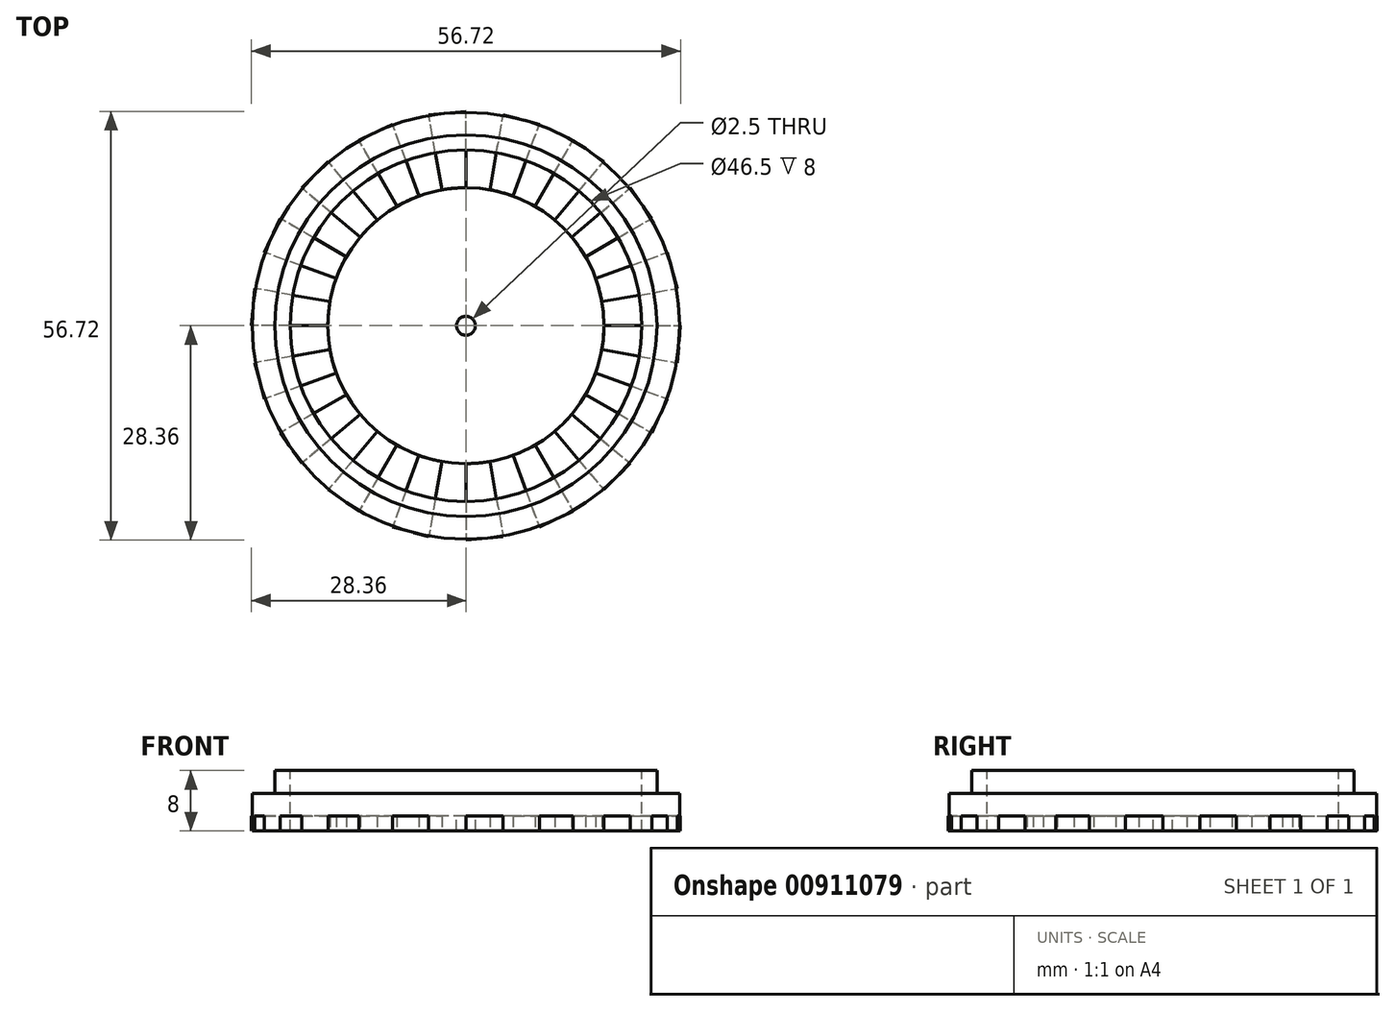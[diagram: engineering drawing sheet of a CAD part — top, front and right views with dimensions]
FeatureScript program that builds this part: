
annotation { "Feature Type Name" : "Feature", "Feature Type Description" : "" }
export const myFeature = defineFeature(function(context is Context, id is Id, definition is map)
    precondition{}
    {
        {
            var Q0;
            Q0=qCreatedBy(makeId("Front.planeOp"),FACE);
            var sketch = newSketch(context, id + "F0", { "sketchPlane" : qUnion([Q0])});
            skLineSegment(sketch, "E0", {"start": v(-103.65, 0) * mm, "end": v(117.55, 0) * mm, "construction": true});
            skLineSegment(sketch, "E1", {"start": v(0, 46.85) * mm, "end": v(0, -57.43) * mm, "construction": true});
            skLineSegment(sketch, "E2.bottom", {"start": v(-1.25, 2) * mm, "end": v(-18.25, 2) * mm});
            skLineSegment(sketch, "E2.top", {"start": v(-1.25, 0) * mm, "end": v(-18.25, 0) * mm});
            skLineSegment(sketch, "E2.left", {"start": v(-1.25, 2) * mm, "end": v(-1.25, 0) * mm});
            skLineSegment(sketch, "E2.right", {"start": v(-18.25, 2) * mm, "end": v(-18.25, 0) * mm});
            skLineSegment(sketch, "E3.top", {"start": v(-23.25, 0) * mm, "end": v(-25.25, 0) * mm});
            skLineSegment(sketch, "E4", {"start": v(-106.04, 1) * mm, "end": v(129.67, 1) * mm, "construction": true});
            skLineSegment(sketch, "E5", {"start": v(-23.25, 0) * mm, "end": v(-23.25, 8) * mm});
            skLineSegment(sketch, "E6", {"start": v(-25.25, 8) * mm, "end": v(-25.25, 0) * mm});
            skLineSegment(sketch, "E7", {"start": v(-25.25, 8) * mm, "end": v(-23.25, 8) * mm});
            skLineSegment(sketch, "E8.bottom", {"start": v(-25.25, 0) * mm, "end": v(-28.25, 0) * mm});
            skLineSegment(sketch, "E8.top", {"start": v(-25.25, 5) * mm, "end": v(-28.25, 5) * mm});
            skLineSegment(sketch, "E8.left", {"start": v(-25.25, 0) * mm, "end": v(-25.25, 5) * mm});
            skLineSegment(sketch, "E8.right", {"start": v(-28.25, 0) * mm, "end": v(-28.25, 5) * mm});
            skLineSegment(sketch, "E9.MirrorCS", {"start": v(1.25, 2) * mm, "end": v(18.25, 2) * mm});
            skLineSegment(sketch, "E10.MirrorCS", {"start": v(1.25, 2) * mm, "end": v(1.25, 0) * mm});
            skLineSegment(sketch, "E11.MirrorCS", {"start": v(28.25, 0) * mm, "end": v(28.25, 5) * mm});
            skLineSegment(sketch, "E12.MirrorCS", {"start": v(25.25, 8) * mm, "end": v(25.25, 0) * mm});
            skLineSegment(sketch, "E13.MirrorCS", {"start": v(1.25, 0) * mm, "end": v(18.25, 0) * mm});
            skLineSegment(sketch, "E14.MirrorCS", {"start": v(25.25, 8) * mm, "end": v(23.25, 8) * mm});
            skLineSegment(sketch, "E15.MirrorCS", {"start": v(25.25, 0) * mm, "end": v(25.25, 5) * mm});
            skLineSegment(sketch, "E16.MirrorCS", {"start": v(25.25, 0) * mm, "end": v(28.25, 0) * mm});
            skLineSegment(sketch, "E17.MirrorCS", {"start": v(25.25, 5) * mm, "end": v(28.25, 5) * mm});
            skLineSegment(sketch, "E18.MirrorCS", {"start": v(18.25, 2) * mm, "end": v(18.25, 0) * mm});
            skLineSegment(sketch, "E19.MirrorCS", {"start": v(23.25, 0) * mm, "end": v(23.25, 8) * mm});
            skLineSegment(sketch, "E20.MirrorCS", {"start": v(23.25, 0) * mm, "end": v(25.25, 0) * mm});
            skSolve(sketch);
        }
        {
            var Q0;
            Q0=makeQuery(id+"F0.imprint","IMPRINT",FACE,{"disambiguationData":[TD([[makeQuery(id+"F0.imprint","IMPRINT",EDGE,{"derivedFrom":sQuery(id+"F0.wireOp",EDGE,"E2.bottom")}),1.0]])]});
            var Q1;
            Q1=makeQuery(id+"F0.imprint","IMPRINT",FACE,{"disambiguationData":[TD([[makeQuery(id+"F0.imprint","IMPRINT",EDGE,{"derivedFrom":sQuery(id+"F0.wireOp",EDGE,"E3.top")}),-1.0]])]});
            var Q2;
            Q2=makeQuery(id+"F0.imprint","IMPRINT",FACE,{"disambiguationData":[TD([[makeQuery(id+"F0.imprint","IMPRINT",EDGE,{"derivedFrom":sQuery(id+"F0.wireOp",EDGE,"E8.bottom")}),-1.0]])]});
            var Q3;
            Q3=sQuery(id+"F0.wireOp",EDGE,"E1");
            revolve(context, id + "F1", {"surfaceOperationType" : NewSurfaceOperationType.NEW, "entities" : qUnion([Q0, Q1, Q2]), "axis" : qUnion([Q3]), "revolveType" : RevolveType.FULL});
        }
        {
            var Q0;
            Q0=makeQuery(id+"F1.opRevolve","SWEPT_FACE",FACE,{"disambiguationData":[OSD([sQuery(id+"F0.wireOp",EDGE,"E2.top")])]});
            var sketch = newSketch(context, id + "F2", { "sketchPlane" : qUnion([Q0])});
            skLineSegment(sketch, "E21", {"start": v(0, -18.25) * mm, "end": v(0, -28.36) * mm});
            skLineSegment(sketch, "E22.1.0", {"start": v(3.17, -17.97) * mm, "end": v(4.92, -27.92) * mm});
            skLineSegment(sketch, "E22.2.0", {"start": v(6.24, -17.15) * mm, "end": v(9.7, -26.65) * mm});
            skLineSegment(sketch, "E22.3.0", {"start": v(9.12, -15.8) * mm, "end": v(14.18, -24.56) * mm});
            skLineSegment(sketch, "E22.4.0", {"start": v(11.73, -13.98) * mm, "end": v(18.23, -21.72) * mm});
            skLineSegment(sketch, "E22.5.0", {"start": v(13.98, -11.73) * mm, "end": v(21.72, -18.23) * mm});
            skLineSegment(sketch, "E22.6.0", {"start": v(15.8, -9.12) * mm, "end": v(24.56, -14.18) * mm});
            skLineSegment(sketch, "E22.7.0", {"start": v(17.15, -6.24) * mm, "end": v(26.65, -9.7) * mm});
            skLineSegment(sketch, "E22.8.0", {"start": v(17.97, -3.17) * mm, "end": v(27.92, -4.92) * mm});
            skLineSegment(sketch, "E22.9.0", {"start": v(18.25, 0) * mm, "end": v(28.36, 0) * mm});
            skLineSegment(sketch, "E22.10.0", {"start": v(17.97, 3.17) * mm, "end": v(27.92, 4.92) * mm});
            skLineSegment(sketch, "E22.11.0", {"start": v(17.15, 6.24) * mm, "end": v(26.65, 9.7) * mm});
            skLineSegment(sketch, "E22.12.0", {"start": v(15.8, 9.13) * mm, "end": v(24.56, 14.18) * mm});
            skLineSegment(sketch, "E22.13.0", {"start": v(13.98, 11.73) * mm, "end": v(21.72, 18.23) * mm});
            skLineSegment(sketch, "E22.14.0", {"start": v(11.73, 13.98) * mm, "end": v(18.23, 21.72) * mm});
            skLineSegment(sketch, "E22.15.0", {"start": v(9.13, 15.8) * mm, "end": v(14.18, 24.56) * mm});
            skLineSegment(sketch, "E22.16.0", {"start": v(6.24, 17.15) * mm, "end": v(9.7, 26.65) * mm});
            skLineSegment(sketch, "E22.17.0", {"start": v(3.17, 17.97) * mm, "end": v(4.92, 27.92) * mm});
            skLineSegment(sketch, "E22.18.0", {"start": v(0, 18.25) * mm, "end": v(0, 28.36) * mm});
            skLineSegment(sketch, "E22.19.0", {"start": v(-3.17, 17.97) * mm, "end": v(-4.92, 27.92) * mm});
            skLineSegment(sketch, "E22.20.0", {"start": v(-6.24, 17.15) * mm, "end": v(-9.7, 26.65) * mm});
            skLineSegment(sketch, "E22.21.0", {"start": v(-9.13, 15.8) * mm, "end": v(-14.18, 24.56) * mm});
            skLineSegment(sketch, "E22.22.0", {"start": v(-11.73, 13.98) * mm, "end": v(-18.23, 21.72) * mm});
            skLineSegment(sketch, "E22.23.0", {"start": v(-13.98, 11.73) * mm, "end": v(-21.72, 18.23) * mm});
            skLineSegment(sketch, "E22.24.0", {"start": v(-15.8, 9.13) * mm, "end": v(-24.56, 14.18) * mm});
            skLineSegment(sketch, "E22.25.0", {"start": v(-17.15, 6.24) * mm, "end": v(-26.65, 9.7) * mm});
            skLineSegment(sketch, "E22.26.0", {"start": v(-17.97, 3.17) * mm, "end": v(-27.92, 4.92) * mm});
            skLineSegment(sketch, "E22.27.0", {"start": v(-18.25, 0) * mm, "end": v(-28.36, 0) * mm});
            skLineSegment(sketch, "E22.28.0", {"start": v(-17.97, -3.17) * mm, "end": v(-27.92, -4.92) * mm});
            skLineSegment(sketch, "E22.29.0", {"start": v(-17.15, -6.24) * mm, "end": v(-26.65, -9.7) * mm});
            skLineSegment(sketch, "E22.30.0", {"start": v(-15.8, -9.12) * mm, "end": v(-24.56, -14.18) * mm});
            skLineSegment(sketch, "E22.31.0", {"start": v(-13.98, -11.73) * mm, "end": v(-21.72, -18.23) * mm});
            skLineSegment(sketch, "E22.32.0", {"start": v(-11.73, -13.98) * mm, "end": v(-18.23, -21.72) * mm});
            skLineSegment(sketch, "E22.33.0", {"start": v(-9.12, -15.8) * mm, "end": v(-14.18, -24.56) * mm});
            skLineSegment(sketch, "E22.34.0", {"start": v(-6.24, -17.15) * mm, "end": v(-9.7, -26.65) * mm});
            skLineSegment(sketch, "E22.35.0", {"start": v(-3.17, -17.97) * mm, "end": v(-4.92, -27.92) * mm});
            skPoint(sketch, "E22.center", {"position": v(0, 0) * mm});
            skLineSegment(sketch, "E23", {"start": v(0, -28.36) * mm, "end": v(-4.92, -27.92) * mm});
            skLineSegment(sketch, "E24", {"start": v(9.7, -26.65) * mm, "end": v(4.92, -27.92) * mm});
            skLineSegment(sketch, "E25", {"start": v(18.23, -21.72) * mm, "end": v(14.18, -24.56) * mm});
            skLineSegment(sketch, "E26", {"start": v(24.56, -14.18) * mm, "end": v(21.72, -18.23) * mm});
            skLineSegment(sketch, "E27", {"start": v(27.92, -4.92) * mm, "end": v(26.65, -9.7) * mm});
            skLineSegment(sketch, "E28", {"start": v(27.92, 4.92) * mm, "end": v(28.36, 0) * mm});
            skLineSegment(sketch, "E29", {"start": v(24.56, 14.18) * mm, "end": v(26.65, 9.7) * mm});
            skLineSegment(sketch, "E30", {"start": v(18.23, 21.72) * mm, "end": v(21.72, 18.23) * mm});
            skLineSegment(sketch, "E31", {"start": v(14.18, 24.56) * mm, "end": v(9.7, 26.65) * mm});
            skLineSegment(sketch, "E32", {"start": v(4.92, 27.92) * mm, "end": v(0, 28.36) * mm});
            skLineSegment(sketch, "E33", {"start": v(-4.92, 27.92) * mm, "end": v(-9.7, 26.65) * mm});
            skLineSegment(sketch, "E34", {"start": v(-14.18, 24.56) * mm, "end": v(-18.23, 21.72) * mm});
            skLineSegment(sketch, "E35", {"start": v(-21.72, 18.23) * mm, "end": v(-24.56, 14.18) * mm});
            skLineSegment(sketch, "E36", {"start": v(-26.65, 9.7) * mm, "end": v(-27.92, 4.92) * mm});
            skLineSegment(sketch, "E37", {"start": v(-28.36, 0) * mm, "end": v(-27.92, -4.92) * mm});
            skLineSegment(sketch, "E38", {"start": v(-26.65, -9.7) * mm, "end": v(-24.56, -14.18) * mm});
            skLineSegment(sketch, "E39", {"start": v(-21.72, -18.23) * mm, "end": v(-18.23, -21.72) * mm});
            skLineSegment(sketch, "E40", {"start": v(-14.18, -24.56) * mm, "end": v(-9.7, -26.65) * mm});
            skSolve(sketch);
        }
        {
            var Q0;
            {var subQ0=sQuery(id+"F2.wireOp",EDGE,"E22.3.0");Q0=makeQuery(id+"F2.imprint","IMPRINT",FACE,{"disambiguationData":[TD([[makeQuery(id+"F2.imprint","IMPRINT",EDGE,{"derivedFrom":subQ0}),1.0]])]});}
            var Q1;
            {var subQ0=sQuery(id+"F2.wireOp",EDGE,"E22.1.0");Q1=makeQuery(id+"F2.imprint","IMPRINT",FACE,{"disambiguationData":[TD([[makeQuery(id+"F2.imprint","IMPRINT",EDGE,{"derivedFrom":subQ0}),1.0]])]});}
            var Q2;
            {var subQ0=sQuery(id+"F2.wireOp",EDGE,"E21");Q2=makeQuery(id+"F2.imprint","IMPRINT",FACE,{"disambiguationData":[TD([[makeQuery(id+"F2.imprint","IMPRINT",EDGE,{"derivedFrom":subQ0}),-1.0]])]});}
            var Q3;
            {var subQ0=sQuery(id+"F2.wireOp",EDGE,"E22.33.0");Q3=makeQuery(id+"F2.imprint","IMPRINT",FACE,{"disambiguationData":[TD([[makeQuery(id+"F2.imprint","IMPRINT",EDGE,{"derivedFrom":subQ0}),1.0]])]});}
            var Q4;
            {var subQ0=sQuery(id+"F2.wireOp",EDGE,"E22.31.0");Q4=makeQuery(id+"F2.imprint","IMPRINT",FACE,{"disambiguationData":[TD([[makeQuery(id+"F2.imprint","IMPRINT",EDGE,{"derivedFrom":subQ0}),1.0]])]});}
            var Q5;
            {var subQ0=sQuery(id+"F2.wireOp",EDGE,"E22.29.0");Q5=makeQuery(id+"F2.imprint","IMPRINT",FACE,{"disambiguationData":[TD([[makeQuery(id+"F2.imprint","IMPRINT",EDGE,{"derivedFrom":subQ0}),1.0]])]});}
            var Q6;
            {var subQ0=sQuery(id+"F2.wireOp",EDGE,"E22.27.0");Q6=makeQuery(id+"F2.imprint","IMPRINT",FACE,{"disambiguationData":[TD([[makeQuery(id+"F2.imprint","IMPRINT",EDGE,{"derivedFrom":subQ0}),1.0]])]});}
            var Q7;
            {var subQ0=sQuery(id+"F2.wireOp",EDGE,"E22.25.0");Q7=makeQuery(id+"F2.imprint","IMPRINT",FACE,{"disambiguationData":[TD([[makeQuery(id+"F2.imprint","IMPRINT",EDGE,{"derivedFrom":subQ0}),1.0]])]});}
            var Q8;
            {var subQ0=sQuery(id+"F2.wireOp",EDGE,"E22.23.0");Q8=makeQuery(id+"F2.imprint","IMPRINT",FACE,{"disambiguationData":[TD([[makeQuery(id+"F2.imprint","IMPRINT",EDGE,{"derivedFrom":subQ0}),1.0]])]});}
            var Q9;
            {var subQ0=sQuery(id+"F2.wireOp",EDGE,"E22.21.0");Q9=makeQuery(id+"F2.imprint","IMPRINT",FACE,{"disambiguationData":[TD([[makeQuery(id+"F2.imprint","IMPRINT",EDGE,{"derivedFrom":subQ0}),1.0]])]});}
            var Q10;
            {var subQ0=sQuery(id+"F2.wireOp",EDGE,"E22.19.0");Q10=makeQuery(id+"F2.imprint","IMPRINT",FACE,{"disambiguationData":[TD([[makeQuery(id+"F2.imprint","IMPRINT",EDGE,{"derivedFrom":subQ0}),1.0]])]});}
            var Q11;
            {var subQ0=sQuery(id+"F2.wireOp",EDGE,"E22.17.0");Q11=makeQuery(id+"F2.imprint","IMPRINT",FACE,{"disambiguationData":[TD([[makeQuery(id+"F2.imprint","IMPRINT",EDGE,{"derivedFrom":subQ0}),1.0]])]});}
            var Q12;
            {var subQ0=sQuery(id+"F2.wireOp",EDGE,"E22.15.0");Q12=makeQuery(id+"F2.imprint","IMPRINT",FACE,{"disambiguationData":[TD([[makeQuery(id+"F2.imprint","IMPRINT",EDGE,{"derivedFrom":subQ0}),1.0]])]});}
            var Q13;
            {var subQ0=sQuery(id+"F2.wireOp",EDGE,"E22.13.0");Q13=makeQuery(id+"F2.imprint","IMPRINT",FACE,{"disambiguationData":[TD([[makeQuery(id+"F2.imprint","IMPRINT",EDGE,{"derivedFrom":subQ0}),1.0]])]});}
            var Q14;
            {var subQ0=sQuery(id+"F2.wireOp",EDGE,"E22.11.0");Q14=makeQuery(id+"F2.imprint","IMPRINT",FACE,{"disambiguationData":[TD([[makeQuery(id+"F2.imprint","IMPRINT",EDGE,{"derivedFrom":subQ0}),1.0]])]});}
            var Q15;
            {var subQ0=sQuery(id+"F2.wireOp",EDGE,"E22.9.0");Q15=makeQuery(id+"F2.imprint","IMPRINT",FACE,{"disambiguationData":[TD([[makeQuery(id+"F2.imprint","IMPRINT",EDGE,{"derivedFrom":subQ0}),1.0]])]});}
            var Q16;
            {var subQ0=sQuery(id+"F2.wireOp",EDGE,"E22.7.0");Q16=makeQuery(id+"F2.imprint","IMPRINT",FACE,{"disambiguationData":[TD([[makeQuery(id+"F2.imprint","IMPRINT",EDGE,{"derivedFrom":subQ0}),1.0]])]});}
            var Q17;
            {var subQ0=sQuery(id+"F2.wireOp",EDGE,"E22.5.0");Q17=makeQuery(id+"F2.imprint","IMPRINT",FACE,{"disambiguationData":[TD([[makeQuery(id+"F2.imprint","IMPRINT",EDGE,{"derivedFrom":subQ0}),1.0]])]});}
            extrude(context, id + "F3", {"entities" : qUnion([Q0, Q1, Q2, Q3, Q4, Q5, Q6, Q7, Q8, Q9, Q10, Q11, Q12, Q13, Q14, Q15, Q16, Q17]), "oppositeDirection" : true, "depth" : 2 * mm, "offsetDistance" : 25 * mm});
        }
    });
